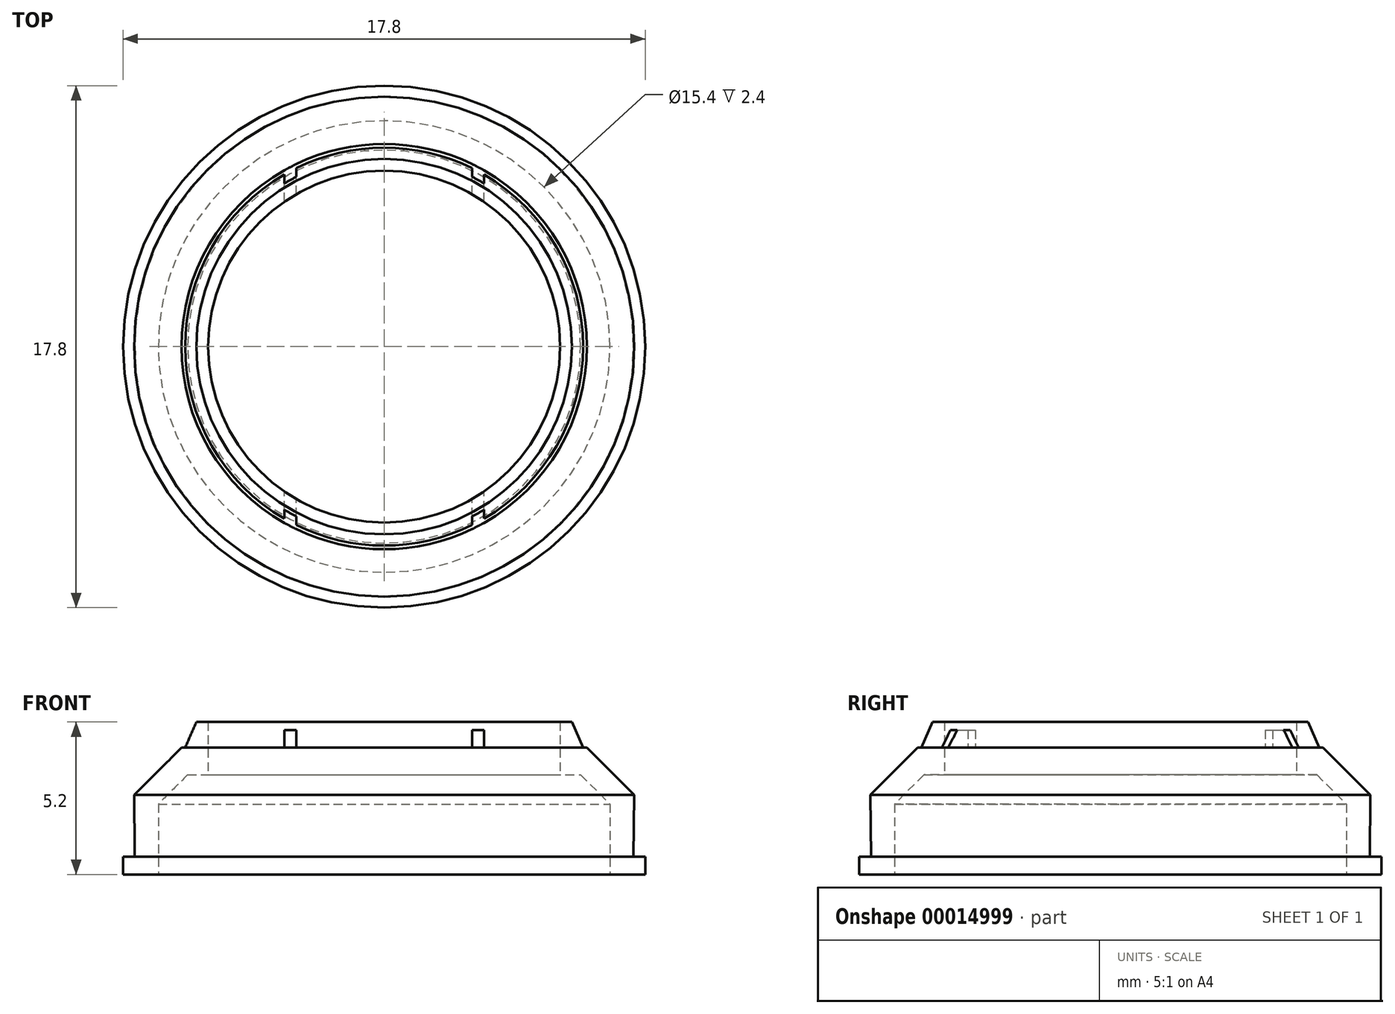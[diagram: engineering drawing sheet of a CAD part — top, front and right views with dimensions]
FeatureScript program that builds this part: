
annotation { "Feature Type Name" : "Feature", "Feature Type Description" : "" }
export const myFeature = defineFeature(function(context is Context, id is Id, definition is map)
    precondition{}
    {
        {
            var Q0;
            Q0=qCreatedBy(makeId("Front.planeOp"),FACE);
            var sketch = newSketch(context, id + "F0", { "sketchPlane" : qUnion([Q0])});
            skLineSegment(sketch, "E0", {"start": v(7.7, 0) * mm, "end": v(8.5, 0) * mm});
            skLineSegment(sketch, "E1", {"start": v(8.52, 2.7) * mm, "end": v(6.91, 4.32) * mm});
            skLineSegment(sketch, "E2", {"start": v(6.91, 4.32) * mm, "end": v(6.78, 4.32) * mm});
            skLineSegment(sketch, "E3", {"start": v(6, 4.2) * mm, "end": v(6, 3.4) * mm});
            skLineSegment(sketch, "E4", {"start": v(6, 3.4) * mm, "end": v(6.7, 3.4) * mm});
            skLineSegment(sketch, "E5", {"start": v(6.7, 3.4) * mm, "end": v(7.7, 2.4) * mm});
            skLineSegment(sketch, "E6", {"start": v(7.7, 2.4) * mm, "end": v(7.7, 0) * mm});
            skPoint(sketch, "E7", {"position": v(8.5, 0.6) * mm});
            skLineSegment(sketch, "E8", {"start": v(8.5, 0.6) * mm, "end": v(8.52, 2.7) * mm});
            skLineSegment(sketch, "E9", {"start": v(8.5, 0.6) * mm, "end": v(8.9, 0.6) * mm});
            skLineSegment(sketch, "E10", {"start": v(8.9, 0.6) * mm, "end": v(8.9, 0) * mm});
            skLineSegment(sketch, "E11", {"start": v(8.9, 0) * mm, "end": v(8.5, 0) * mm});
            skLineSegment(sketch, "E12", {"start": v(6, 4.2) * mm, "end": v(6, 5.2) * mm});
            skLineSegment(sketch, "E13", {"start": v(6, 5.2) * mm, "end": v(6.4, 5.2) * mm});
            skLineSegment(sketch, "E14", {"start": v(6.4, 5.2) * mm, "end": v(6.78, 4.32) * mm});
            skSolve(sketch);
        }
        {
            var Q0;
            Q0=qCreatedBy(makeId("Right.planeOp"),FACE);
            var sketch = newSketch(context, id + "F1", { "sketchPlane" : qUnion([Q0])});
            skLineSegment(sketch, "E15", {"start": v(0, 0) * mm, "end": v(0, 74.88) * mm});
            skSolve(sketch);
        }
        {
            var Q0;
            Q0=makeQuery(id+"F0.imprint","IMPRINT",FACE,{"disambiguationData":[TD([[makeQuery(id+"F0.imprint","IMPRINT",EDGE,{"derivedFrom":sQuery(id+"F0.wireOp",EDGE,"E0")}),1.0]])]});
            var Q1;
            Q1=sQuery(id+"F1.wireOp",EDGE,"E15");
            revolve(context, id + "F2", {"entities" : qUnion([Q0]), "axis" : qUnion([Q1]), "revolveType" : RevolveType.FULL});
        }
        {
            var Q0;
            Q0=qCreatedBy(makeId("Front.planeOp"),FACE);
            var sketch = newSketch(context, id + "F3", { "sketchPlane" : qUnion([Q0])});
            skLineSegment(sketch, "E16.rect.bottom", {"start": v(-3, 4.32) * mm, "end": v(-3.4, 4.32) * mm});
            skLineSegment(sketch, "E16.rect.top", {"start": v(-3, 4.92) * mm, "end": v(-3.4, 4.92) * mm});
            skLineSegment(sketch, "E16.rect.left", {"start": v(-3, 4.32) * mm, "end": v(-3, 4.92) * mm});
            skLineSegment(sketch, "E16.rect.right", {"start": v(-3.4, 4.32) * mm, "end": v(-3.4, 4.92) * mm});
            skPoint(sketch, "E16.rect.middle", {"position": v(-3.2, 4.62) * mm});
            skLineSegment(sketch, "E17.rect.bottom", {"start": v(3.4, 4.32) * mm, "end": v(3, 4.32) * mm});
            skLineSegment(sketch, "E17.rect.top", {"start": v(3.4, 4.92) * mm, "end": v(3, 4.92) * mm});
            skLineSegment(sketch, "E17.rect.left", {"start": v(3.4, 4.32) * mm, "end": v(3.4, 4.92) * mm});
            skLineSegment(sketch, "E17.rect.right", {"start": v(3, 4.32) * mm, "end": v(3, 4.92) * mm});
            skPoint(sketch, "E17.rect.middle", {"position": v(3.2, 4.62) * mm});
            skSolve(sketch);
        }
        {
            var Q0;
            Q0=makeQuery(id+"F3.imprint","IMPRINT",FACE,{"disambiguationData":[TD([[makeQuery(id+"F3.imprint","IMPRINT",EDGE,{"derivedFrom":sQuery(id+"F3.wireOp",EDGE,"E16.rect.bottom")}),-1.0]])]});
            var Q1;
            Q1=makeQuery(id+"F3.imprint","IMPRINT",FACE,{"disambiguationData":[TD([[makeQuery(id+"F3.imprint","IMPRINT",EDGE,{"derivedFrom":sQuery(id+"F3.wireOp",EDGE,"E17.rect.bottom")}),-1.0]])]});
            extrude(context, id + "F4", {"entities" : qUnion([Q0, Q1]), "endBound" : BoundingType.SYMMETRIC, "depth" : 25 * mm});
        }
        {
            var Q0;
            Q0=makeQuery(id+"F4.opExtrude","SWEPT_BODY",BODY,{"disambiguationData":[OSD([sQuery(id+"F3.wireOp",EDGE,"E16.rect.bottom"),sQuery(id+"F3.wireOp",EDGE,"E16.rect.top"),sQuery(id+"F3.wireOp",EDGE,"E16.rect.left"),sQuery(id+"F3.wireOp",EDGE,"E16.rect.right")])]});
            var Q1;
            Q1=makeQuery(id+"F4.opExtrude","SWEPT_BODY",BODY,{"disambiguationData":[OSD([sQuery(id+"F3.wireOp",EDGE,"E17.rect.bottom"),sQuery(id+"F3.wireOp",EDGE,"E17.rect.top"),sQuery(id+"F3.wireOp",EDGE,"E17.rect.left"),sQuery(id+"F3.wireOp",EDGE,"E17.rect.right")])]});
            var Q2;
            Q2=makeQuery(id+"F2.opRevolve","SWEPT_BODY",BODY,{"disambiguationData":[OSD([sQuery(id+"F0.wireOp",EDGE,"E0"),sQuery(id+"F0.wireOp",EDGE,"E1"),sQuery(id+"F0.wireOp",EDGE,"E2"),sQuery(id+"F0.wireOp",EDGE,"E3"),sQuery(id+"F0.wireOp",EDGE,"E4"),sQuery(id+"F0.wireOp",EDGE,"E5"),sQuery(id+"F0.wireOp",EDGE,"E6"),sQuery(id+"F0.wireOp",EDGE,"E8"),sQuery(id+"F0.wireOp",EDGE,"E9"),sQuery(id+"F0.wireOp",EDGE,"E10"),sQuery(id+"F0.wireOp",EDGE,"E11"),sQuery(id+"F0.wireOp",EDGE,"E12"),sQuery(id+"F0.wireOp",EDGE,"E13"),sQuery(id+"F0.wireOp",EDGE,"E14")])]});
            booleanBodies(context, id + "F5", {"operationType" : BooleanOperationType.SUBTRACTION, "tools" : qUnion([Q0, Q1]), "targets" : qUnion([Q2])});
        }
    });
